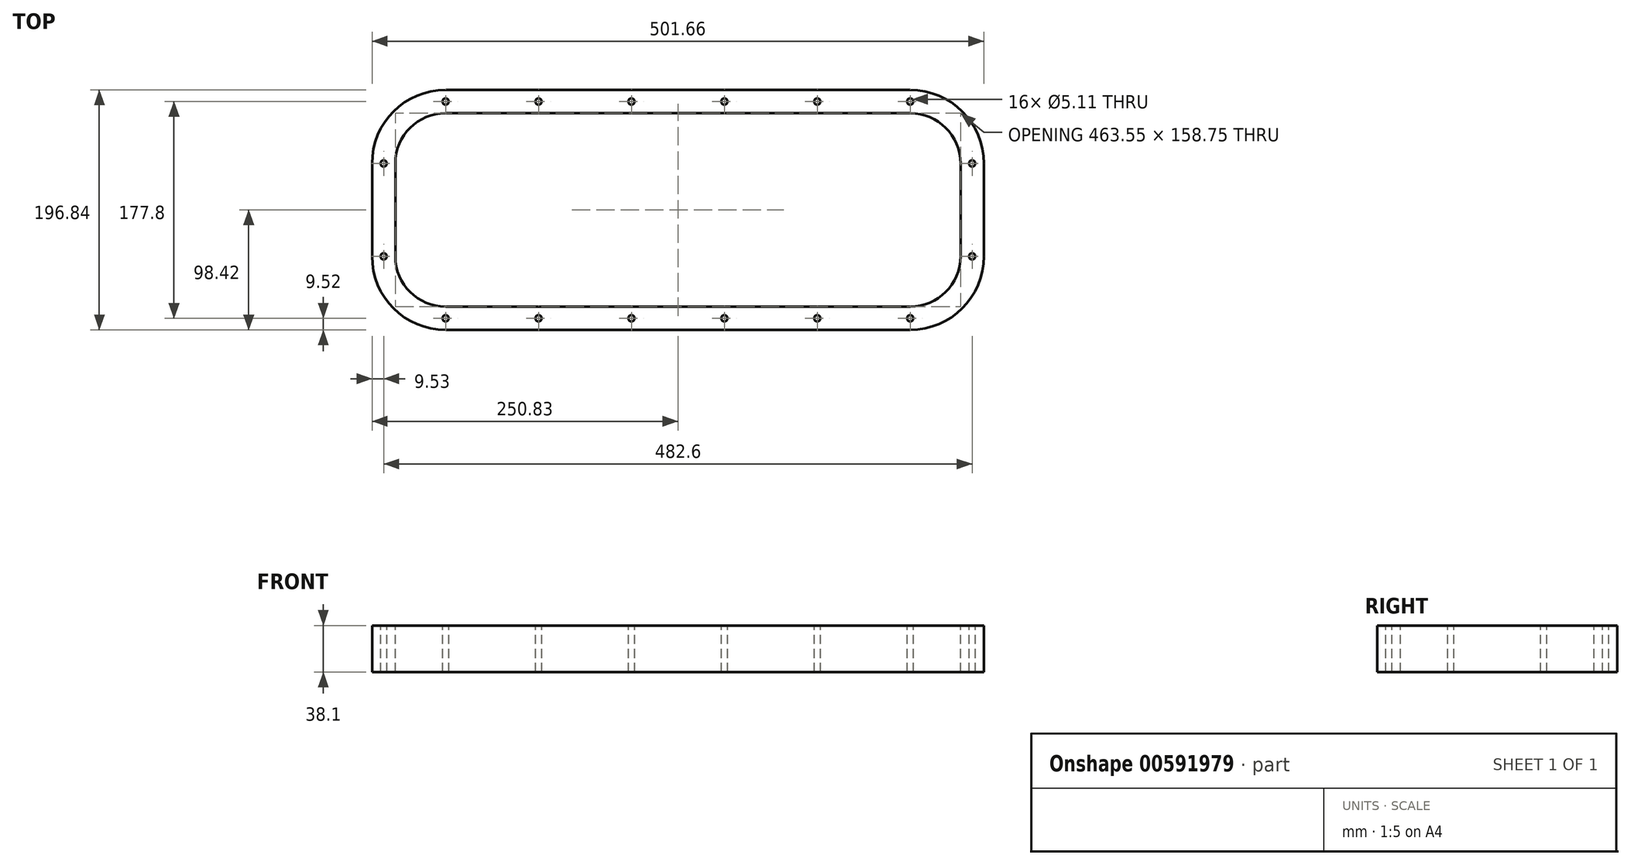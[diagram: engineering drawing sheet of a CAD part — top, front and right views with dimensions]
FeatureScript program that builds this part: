
annotation { "Feature Type Name" : "Feature", "Feature Type Description" : "" }
export const myFeature = defineFeature(function(context is Context, id is Id, definition is map)
    precondition{}
    {
        {
            var Q0;
            Q0=qCreatedBy(makeId("Top.planeOp"),FACE);
            var sketch = newSketch(context, id + "F0", { "sketchPlane" : qUnion([Q0])});
            skLineSegment(sketch, "E0.bottom", {"start": v(190.5, 98.43) * mm, "end": v(-190.5, 98.43) * mm});
            skLineSegment(sketch, "E0.top", {"start": v(190.5, -98.43) * mm, "end": v(-190.5, -98.43) * mm});
            skLineSegment(sketch, "E0.left", {"start": v(250.83, 38.1) * mm, "end": v(250.83, -38.1) * mm});
            skLineSegment(sketch, "E0.right", {"start": v(-250.83, 38.1) * mm, "end": v(-250.83, -38.1) * mm});
            skPoint(sketch, "E0.middle", {"position": v(0, 0) * mm});
            skPoint(sketch, "E1.visualSharp", {"position": v(-250.83, 98.43) * mm});
            skArc(sketch, "E1.filletArc", {"start": v(-190.5, 98.42) * mm, "mid": v(-233.16, 80.76) * mm, "end": v(-250.83, 38.1) * mm});
            skPoint(sketch, "E2.visualSharp", {"position": v(-250.83, -98.43) * mm});
            skArc(sketch, "E2.filletArc", {"start": v(-250.83, -38.1) * mm, "mid": v(-233.16, -80.76) * mm, "end": v(-190.5, -98.43) * mm});
            skPoint(sketch, "E3.visualSharp", {"position": v(250.83, -98.43) * mm});
            skArc(sketch, "E3.filletArc", {"start": v(190.5, -98.43) * mm, "mid": v(233.16, -80.76) * mm, "end": v(250.83, -38.1) * mm});
            skPoint(sketch, "E4.visualSharp", {"position": v(250.83, 98.43) * mm});
            skArc(sketch, "E4.filletArc", {"start": v(250.83, 38.1) * mm, "mid": v(233.16, 80.76) * mm, "end": v(190.5, 98.43) * mm});
            skSolve(sketch);
        }
        {
            var Q0;
            Q0=makeQuery(id+"F0.imprint","IMPRINT",FACE,{"disambiguationData":[TD([[makeQuery(id+"F0.imprint","IMPRINT",EDGE,{"derivedFrom":sQuery(id+"F0.wireOp",EDGE,"E0.bottom")}),1.0]])]});
            extrude(context, id + "F1", {"entities" : qUnion([Q0]), "endBound" : BoundingType.SYMMETRIC, "depth" : 38.1 * mm, "offsetDistance" : 25.4 * mm});
        }
        {
            var Q0;
            Q0=makeQuery(id+"F1.opExtrude","CAP_FACE",FACE,{"disambiguationData":[OSD([sQuery(id+"F0.wireOp",EDGE,"E0.bottom"),sQuery(id+"F0.wireOp",EDGE,"E0.top"),sQuery(id+"F0.wireOp",EDGE,"E0.left"),sQuery(id+"F0.wireOp",EDGE,"E0.right"),sQuery(id+"F0.wireOp",EDGE,"E1.filletArc"),sQuery(id+"F0.wireOp",EDGE,"E2.filletArc"),sQuery(id+"F0.wireOp",EDGE,"E3.filletArc"),sQuery(id+"F0.wireOp",EDGE,"E4.filletArc")])],"isStart":false});
            var sketch = newSketch(context, id + "F2", { "sketchPlane" : qUnion([Q0])});
            skLineSegment(sketch, "E5.bottom", {"start": v(-190.5, 79.37) * mm, "end": v(190.5, 79.37) * mm});
            skLineSegment(sketch, "E5.top", {"start": v(-190.5, -79.37) * mm, "end": v(190.5, -79.37) * mm});
            skLineSegment(sketch, "E5.left", {"start": v(-231.78, 38.1) * mm, "end": v(-231.78, -38.1) * mm});
            skLineSegment(sketch, "E5.right", {"start": v(231.78, 38.1) * mm, "end": v(231.78, -38.1) * mm});
            skPoint(sketch, "E5.middle", {"position": v(0, 0) * mm});
            skPoint(sketch, "E6.visualSharp", {"position": v(-231.78, 79.37) * mm});
            skArc(sketch, "E6.filletArc", {"start": v(-190.5, 79.37) * mm, "mid": v(-219.69, 67.29) * mm, "end": v(-231.78, 38.1) * mm});
            skPoint(sketch, "E7.visualSharp", {"position": v(-231.78, -79.37) * mm});
            skArc(sketch, "E7.filletArc", {"start": v(-231.78, -38.1) * mm, "mid": v(-219.69, -67.29) * mm, "end": v(-190.5, -79.37) * mm});
            skPoint(sketch, "E8.visualSharp", {"position": v(231.78, -79.37) * mm});
            skArc(sketch, "E8.filletArc", {"start": v(190.5, -79.37) * mm, "mid": v(219.69, -67.29) * mm, "end": v(231.78, -38.1) * mm});
            skPoint(sketch, "E9.visualSharp", {"position": v(231.78, 79.37) * mm});
            skArc(sketch, "E9.filletArc", {"start": v(231.78, 38.1) * mm, "mid": v(219.69, 67.29) * mm, "end": v(190.5, 79.37) * mm});
            skSolve(sketch);
        }
        {
            var Q0;
            Q0=makeQuery(id+"F2.imprint","IMPRINT",FACE,{"disambiguationData":[TD([[makeQuery(id+"F2.imprint","IMPRINT",EDGE,{"derivedFrom":sQuery(id+"F2.wireOp",EDGE,"E5.bottom")}),-1.0]])]});
            extrude(context, id + "F3", {"entities" : qUnion([Q0]), "operationType" : NewBodyOperationType.REMOVE, "endBound" : BoundingType.THROUGH_ALL, "oppositeDirection" : true, "depth" : 25.4 * mm, "offsetDistance" : 25.4 * mm});
        }
        {
            var Q0;
            Q0=makeQuery(id+"F1.opExtrude","CAP_FACE",FACE,{"disambiguationData":[OSD([sQuery(id+"F0.wireOp",EDGE,"E0.bottom"),sQuery(id+"F0.wireOp",EDGE,"E0.top"),sQuery(id+"F0.wireOp",EDGE,"E0.left"),sQuery(id+"F0.wireOp",EDGE,"E0.right"),sQuery(id+"F0.wireOp",EDGE,"E1.filletArc"),sQuery(id+"F0.wireOp",EDGE,"E2.filletArc"),sQuery(id+"F0.wireOp",EDGE,"E3.filletArc"),sQuery(id+"F0.wireOp",EDGE,"E4.filletArc")])],"isStart":false});
            var sketch = newSketch(context, id + "F4", { "sketchPlane" : qUnion([Q0])});
            skArc(sketch, "E10.0", {"start": v(-190.5, 88.9) * mm, "mid": v(-226.42, 74.02) * mm, "end": v(-241.3, 38.1) * mm, "construction": true});
            skLineSegment(sketch, "E10.1", {"start": v(-241.3, 38.1) * mm, "end": v(-241.3, -38.1) * mm, "construction": true});
            skLineSegment(sketch, "E10.2", {"start": v(-190.5, 88.9) * mm, "end": v(190.5, 88.9) * mm, "construction": true});
            skArc(sketch, "E10.3", {"start": v(-241.3, -38.1) * mm, "mid": v(-226.42, -74.02) * mm, "end": v(-190.5, -88.9) * mm, "construction": true});
            skArc(sketch, "E10.4", {"start": v(241.3, 38.1) * mm, "mid": v(226.42, 74.02) * mm, "end": v(190.5, 88.9) * mm, "construction": true});
            skLineSegment(sketch, "E10.5", {"start": v(241.3, 38.1) * mm, "end": v(241.3, -38.1) * mm, "construction": true});
            skArc(sketch, "E10.6", {"start": v(190.5, -88.9) * mm, "mid": v(226.42, -74.02) * mm, "end": v(241.3, -38.1) * mm, "construction": true});
            skLineSegment(sketch, "E10.7", {"start": v(-190.5, -88.9) * mm, "end": v(190.5, -88.9) * mm, "construction": true});
            skCircle(sketch, "E11", {"center": v(-190.5, 88.9) * mm, "radius": 2.55 * mm});
            skCircle(sketch, "E12.0.1.0", {"center": v(-190.5, -88.9) * mm, "radius": 2.55 * mm});
            skCircle(sketch, "E12.1.0.0", {"center": v(-114.3, 88.9) * mm, "radius": 2.55 * mm});
            skCircle(sketch, "E12.1.1.0", {"center": v(-114.3, -88.9) * mm, "radius": 2.55 * mm});
            skCircle(sketch, "E12.2.0.0", {"center": v(-38.1, 88.9) * mm, "radius": 2.55 * mm});
            skCircle(sketch, "E12.2.1.0", {"center": v(-38.1, -88.9) * mm, "radius": 2.55 * mm});
            skCircle(sketch, "E12.3.0.0", {"center": v(38.1, 88.9) * mm, "radius": 2.55 * mm});
            skCircle(sketch, "E12.3.1.0", {"center": v(38.1, -88.9) * mm, "radius": 2.55 * mm});
            skCircle(sketch, "E12.4.0.0", {"center": v(114.3, 88.9) * mm, "radius": 2.55 * mm});
            skCircle(sketch, "E12.4.1.0", {"center": v(114.3, -88.9) * mm, "radius": 2.55 * mm});
            skCircle(sketch, "E12.5.0.0", {"center": v(190.5, 88.9) * mm, "radius": 2.55 * mm});
            skCircle(sketch, "E12.5.1.0", {"center": v(190.5, -88.9) * mm, "radius": 2.55 * mm});
            skLineSegment(sketch, "E12.direction1", {"start": v(-190.5, 88.9) * mm, "end": v(-114.3, 88.9) * mm, "construction": true});
            skLineSegment(sketch, "E12.direction2", {"start": v(-190.5, 88.9) * mm, "end": v(-190.5, -88.9) * mm, "construction": true});
            skCircle(sketch, "E13", {"center": v(-241.3, 38.1) * mm, "radius": 2.55 * mm});
            skCircle(sketch, "E14.0.1.0", {"center": v(-241.3, -38.1) * mm, "radius": 2.55 * mm});
            skCircle(sketch, "E14.1.0.0", {"center": v(241.3, 38.1) * mm, "radius": 2.55 * mm});
            skCircle(sketch, "E14.1.1.0", {"center": v(241.3, -38.1) * mm, "radius": 2.55 * mm});
            skLineSegment(sketch, "E14.direction1", {"start": v(-241.3, 38.1) * mm, "end": v(241.3, 38.1) * mm, "construction": true});
            skSolve(sketch);
        }
        {
            var Q0;
            Q0=makeQuery(id+"F4.imprint","IMPRINT",FACE,{"disambiguationData":[TD([[makeQuery(id+"F4.imprint","IMPRINT",EDGE,{"derivedFrom":sQuery(id+"F4.wireOp",EDGE,"E11")}),1.0]])]});
            var Q1;
            Q1=makeQuery(id+"F4.imprint","IMPRINT",FACE,{"disambiguationData":[TD([[makeQuery(id+"F4.imprint","IMPRINT",EDGE,{"derivedFrom":sQuery(id+"F4.wireOp",EDGE,"E12.2.0.0")}),1.0]])]});
            var Q2;
            Q2=makeQuery(id+"F4.imprint","IMPRINT",FACE,{"disambiguationData":[TD([[makeQuery(id+"F4.imprint","IMPRINT",EDGE,{"derivedFrom":sQuery(id+"F4.wireOp",EDGE,"E12.1.0.0")}),1.0]])]});
            var Q3;
            Q3=makeQuery(id+"F4.imprint","IMPRINT",FACE,{"disambiguationData":[TD([[makeQuery(id+"F4.imprint","IMPRINT",EDGE,{"derivedFrom":sQuery(id+"F4.wireOp",EDGE,"E12.3.0.0")}),1.0]])]});
            var Q4;
            Q4=makeQuery(id+"F4.imprint","IMPRINT",FACE,{"disambiguationData":[TD([[makeQuery(id+"F4.imprint","IMPRINT",EDGE,{"derivedFrom":sQuery(id+"F4.wireOp",EDGE,"E12.4.0.0")}),1.0]])]});
            var Q5;
            Q5=makeQuery(id+"F4.imprint","IMPRINT",FACE,{"disambiguationData":[TD([[makeQuery(id+"F4.imprint","IMPRINT",EDGE,{"derivedFrom":sQuery(id+"F4.wireOp",EDGE,"E12.5.0.0")}),1.0]])]});
            var Q6;
            Q6=makeQuery(id+"F4.imprint","IMPRINT",FACE,{"disambiguationData":[TD([[makeQuery(id+"F4.imprint","IMPRINT",EDGE,{"derivedFrom":sQuery(id+"F4.wireOp",EDGE,"E14.1.0.0")}),1.0]])]});
            var Q7;
            Q7=makeQuery(id+"F4.imprint","IMPRINT",FACE,{"disambiguationData":[TD([[makeQuery(id+"F4.imprint","IMPRINT",EDGE,{"derivedFrom":sQuery(id+"F4.wireOp",EDGE,"E14.1.1.0")}),1.0]])]});
            var Q8;
            Q8=makeQuery(id+"F4.imprint","IMPRINT",FACE,{"disambiguationData":[TD([[makeQuery(id+"F4.imprint","IMPRINT",EDGE,{"derivedFrom":sQuery(id+"F4.wireOp",EDGE,"E12.5.1.0")}),1.0]])]});
            var Q9;
            Q9=makeQuery(id+"F4.imprint","IMPRINT",FACE,{"disambiguationData":[TD([[makeQuery(id+"F4.imprint","IMPRINT",EDGE,{"derivedFrom":sQuery(id+"F4.wireOp",EDGE,"E12.4.1.0")}),1.0]])]});
            var Q10;
            Q10=makeQuery(id+"F4.imprint","IMPRINT",FACE,{"disambiguationData":[TD([[makeQuery(id+"F4.imprint","IMPRINT",EDGE,{"derivedFrom":sQuery(id+"F4.wireOp",EDGE,"E12.3.1.0")}),1.0]])]});
            var Q11;
            Q11=makeQuery(id+"F4.imprint","IMPRINT",FACE,{"disambiguationData":[TD([[makeQuery(id+"F4.imprint","IMPRINT",EDGE,{"derivedFrom":sQuery(id+"F4.wireOp",EDGE,"E12.2.1.0")}),1.0]])]});
            var Q12;
            Q12=makeQuery(id+"F4.imprint","IMPRINT",FACE,{"disambiguationData":[TD([[makeQuery(id+"F4.imprint","IMPRINT",EDGE,{"derivedFrom":sQuery(id+"F4.wireOp",EDGE,"E12.1.1.0")}),1.0]])]});
            var Q13;
            Q13=makeQuery(id+"F4.imprint","IMPRINT",FACE,{"disambiguationData":[TD([[makeQuery(id+"F4.imprint","IMPRINT",EDGE,{"derivedFrom":sQuery(id+"F4.wireOp",EDGE,"E12.0.1.0")}),1.0]])]});
            var Q14;
            Q14=makeQuery(id+"F4.imprint","IMPRINT",FACE,{"disambiguationData":[TD([[makeQuery(id+"F4.imprint","IMPRINT",EDGE,{"derivedFrom":sQuery(id+"F4.wireOp",EDGE,"E14.0.1.0")}),1.0]])]});
            var Q15;
            Q15=makeQuery(id+"F4.imprint","IMPRINT",FACE,{"disambiguationData":[TD([[makeQuery(id+"F4.imprint","IMPRINT",EDGE,{"derivedFrom":sQuery(id+"F4.wireOp",EDGE,"E13")}),1.0]])]});
            var Q16;
            Q16=sQuery(id+"F4.wireOp",EDGE,"E11");
            extrude(context, id + "F5", {"entities" : qUnion([Q0, Q1, Q2, Q3, Q4, Q5, Q6, Q7, Q8, Q9, Q10, Q11, Q12, Q13, Q14, Q15]), "operationType" : NewBodyOperationType.REMOVE, "surfaceEntities" : qUnion([Q16]), "endBound" : BoundingType.THROUGH_ALL, "oppositeDirection" : true, "depth" : 25.4 * mm, "offsetDistance" : 25.4 * mm});
        }
        {
            var Q0;
            Q0=makeQuery(id+"F1.opExtrude","SWEPT_BODY",BODY,{"disambiguationData":[OSD([sQuery(id+"F0.wireOp",EDGE,"E0.bottom"),sQuery(id+"F0.wireOp",EDGE,"E0.top"),sQuery(id+"F0.wireOp",EDGE,"E0.left"),sQuery(id+"F0.wireOp",EDGE,"E0.right"),sQuery(id+"F0.wireOp",EDGE,"E1.filletArc"),sQuery(id+"F0.wireOp",EDGE,"E2.filletArc"),sQuery(id+"F0.wireOp",EDGE,"E3.filletArc"),sQuery(id+"F0.wireOp",EDGE,"E4.filletArc")])]});
            transform(context, id + "F6", {"entities" : qUnion([Q0]), "transformType" : TransformType.COPY});
        }
        {
            var Q0;
            Q0=makeQuery(id+"F6.opPattern","COPY",BODY,{"derivedFrom":makeQuery(id+"F1.opExtrude","SWEPT_BODY",BODY,{"disambiguationData":[OSD([sQuery(id+"F0.wireOp",EDGE,"E0.bottom"),sQuery(id+"F0.wireOp",EDGE,"E0.top"),sQuery(id+"F0.wireOp",EDGE,"E0.left"),sQuery(id+"F0.wireOp",EDGE,"E0.right"),sQuery(id+"F0.wireOp",EDGE,"E1.filletArc"),sQuery(id+"F0.wireOp",EDGE,"E2.filletArc"),sQuery(id+"F0.wireOp",EDGE,"E3.filletArc"),sQuery(id+"F0.wireOp",EDGE,"E4.filletArc")])]}),"instanceName":"1"});
            deleteBodies(context, id + "F7", {"entities" : qUnion([Q0])});
        }
    });
